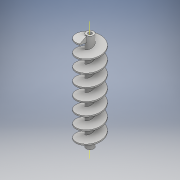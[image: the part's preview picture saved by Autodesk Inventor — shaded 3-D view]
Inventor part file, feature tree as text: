
AUTODESK INVENTOR PART (.ipt)
format: ipt  version: 2017 (Build 210142000, 142)  size: 260,608 bytes
history: native  units: mm
features: extrude x2, helix x2, sketch x2
ambient origin geometry x8: Origin, YZ Plane, XZ Plane, XY Plane, X Axis, Y Axis, Z Axis, Center Point
bodies: Solid1 (feature_tree)
feature tree (6):
  extrude  "Axis"  Depth=75.248711mm
  helix  "Coil1"  [1 undecoded]
  extrude  "Extrusion2"  [1 undecoded]
  sketch  "Sketch1"  dims[d2=0.0mm d8=75.248711mm]
  helix  "CoilSketch"  [1 undecoded]
  sketch  "Sketch3"  dims[d10=0.0mm d11=90.0deg d12=90.0deg d13=0.0mm d14=0.0mm d18=0.0mm]
note: 3 required parameter values undecoded (feature->parameter linkage not recoverable at this tier; creation-order binding heuristic only, values carry confidence <= 0.55)
